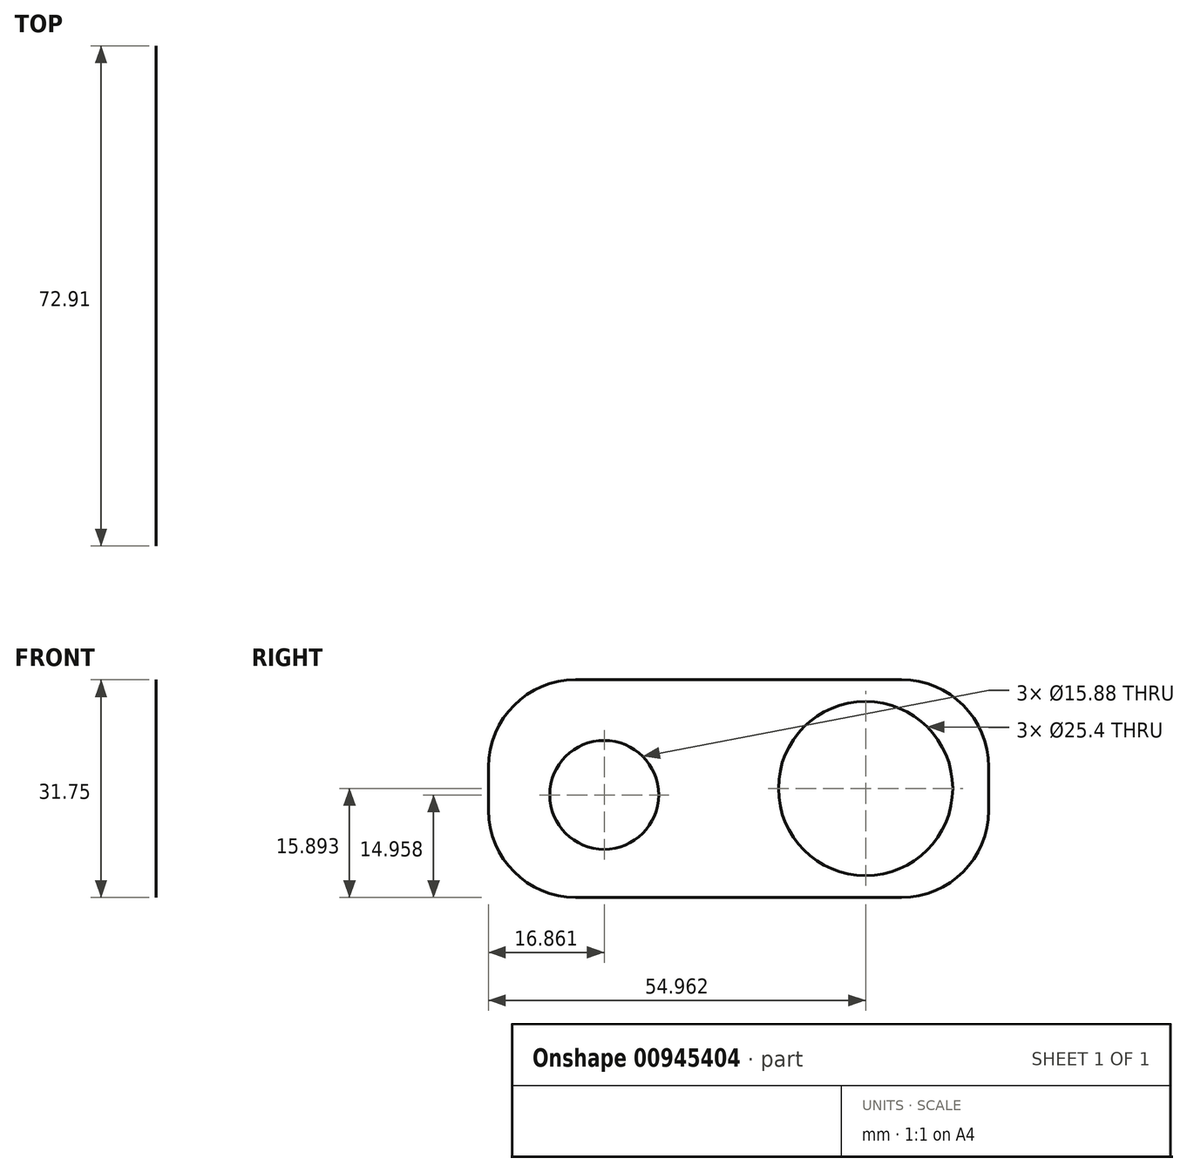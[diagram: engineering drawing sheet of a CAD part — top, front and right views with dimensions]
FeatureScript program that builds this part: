
annotation { "Feature Type Name" : "Feature", "Feature Type Description" : "" }
export const myFeature = defineFeature(function(context is Context, id is Id, definition is map)
    precondition{}
    {
        {
            var Q0;
            Q0=qCreatedBy(makeId("Right.planeOp"),FACE);
            var sketch = newSketch(context, id + "F0", { "sketchPlane" : qUnion([Q0])});
            skCircle(sketch, "E0", {"center": v(-7.35, 16.92) * mm, "radius": 7.94 * mm});
            skCircle(sketch, "E1", {"center": v(30.75, 17.85) * mm, "radius": 12.7 * mm});
            skLineSegment(sketch, "E2.bottom", {"start": v(-11.5, 33.71) * mm, "end": v(36, 33.71) * mm});
            skLineSegment(sketch, "E2.top", {"start": v(-11.5, 1.96) * mm, "end": v(36, 1.96) * mm});
            skLineSegment(sketch, "E2.left", {"start": v(-24.2, 21.01) * mm, "end": v(-24.2, 14.66) * mm});
            skLineSegment(sketch, "E2.right", {"start": v(48.7, 21.01) * mm, "end": v(48.7, 14.66) * mm});
            skPoint(sketch, "E3.visualSharp", {"position": v(-24.2, 33.71) * mm});
            skArc(sketch, "E3.filletArc", {"start": v(-11.5, 33.71) * mm, "mid": v(-20.49, 30) * mm, "end": v(-24.2, 21.01) * mm});
            skPoint(sketch, "E4.visualSharp", {"position": v(-24.2, 1.96) * mm});
            skArc(sketch, "E4.filletArc", {"start": v(-24.2, 14.66) * mm, "mid": v(-20.49, 5.68) * mm, "end": v(-11.5, 1.96) * mm});
            skPoint(sketch, "E5.visualSharp", {"position": v(48.7, 33.71) * mm});
            skArc(sketch, "E5.filletArc", {"start": v(48.7, 21.01) * mm, "mid": v(44.98, 30) * mm, "end": v(36, 33.71) * mm});
            skPoint(sketch, "E6.visualSharp", {"position": v(48.7, 1.96) * mm});
            skArc(sketch, "E6.filletArc", {"start": v(36, 1.96) * mm, "mid": v(44.98, 5.68) * mm, "end": v(48.7, 14.66) * mm});
            skSolve(sketch);
        }
        {
            var Q0;
            Q0=makeQuery(id+"F0.imprint","IMPRINT",FACE,{"disambiguationData":[TD([[makeQuery(id+"F0.imprint","IMPRINT",EDGE,{"derivedFrom":sQuery(id+"F0.wireOp",EDGE,"E0")}),-1.0]])]});
            extrude(context, id + "F1", {"entities" : qUnion([Q0]), "depth" : 1 / 203.2 * mm, "offsetDistance" : 25.4 * mm});
        }
    });
